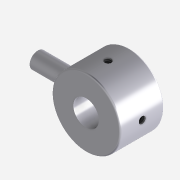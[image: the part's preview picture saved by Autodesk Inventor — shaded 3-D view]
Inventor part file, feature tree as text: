
AUTODESK INVENTOR PART (.ipt)
format: ipt  version: 2018.2 (Build 222227000, 227)  size: 198,144 bytes
history: native  units: mm
features: sketch x4, extrude x2, hole x2, plane x2, fillet x2, pattern_circular x1, shell x1
ambient origin geometry x8: Origin, YZ Plane, XZ Plane, XY Plane, X Axis, Y Axis, Z Axis, Center Point
bodies: Solid1 (feature_tree)
feature tree (14):
  extrude  "Extrusion1"  Depth=14.0mm TaperAngle=0.0deg
  hole  "Hole1"  [1 undecoded]
  plane  "Work Plane2"
  hole  "Hole2"  [1 undecoded]
  pattern_circular  "Circular Pattern1"  Count=3 Angle=180.0deg
  shell  "Shell2"  Thickness=1.5mm
  plane  "Work Plane1"
  extrude  "Extrusion2"  Depth=0.5mm
  fillet  "Fillet1"  [1 undecoded]
  fillet  "Fillet2"  [1 undecoded]
  sketch  "Sketch1"  dims[d0=22.0mm d1=14.0mm d2=0.0mm]
  sketch  "Sketch2"  dims[d3=8.2mm d4=6.0mm d5=4.0mm d6=2.0mm d7=90.0deg d8=8.0mm d9=20.594885mm d10=5.2mm]
  sketch  "Sketch3"  dims[d11=11.5mm d12=0.0mm d13=1.0mm d14=0.0mm]
  sketch  "Sketch4"  dims[d15=0.5mm d16=2.156mm d17=5.69mm d18=4.0mm d19=2.0mm d20=90.0deg d21=8.865mm d22=20.594885mm d23=30.0mm d24=180.0deg d28=1.5mm d29=0.5mm]
note: 4 required parameter values undecoded (feature->parameter linkage not recoverable at this tier; creation-order binding heuristic only, values carry confidence <= 0.55)
